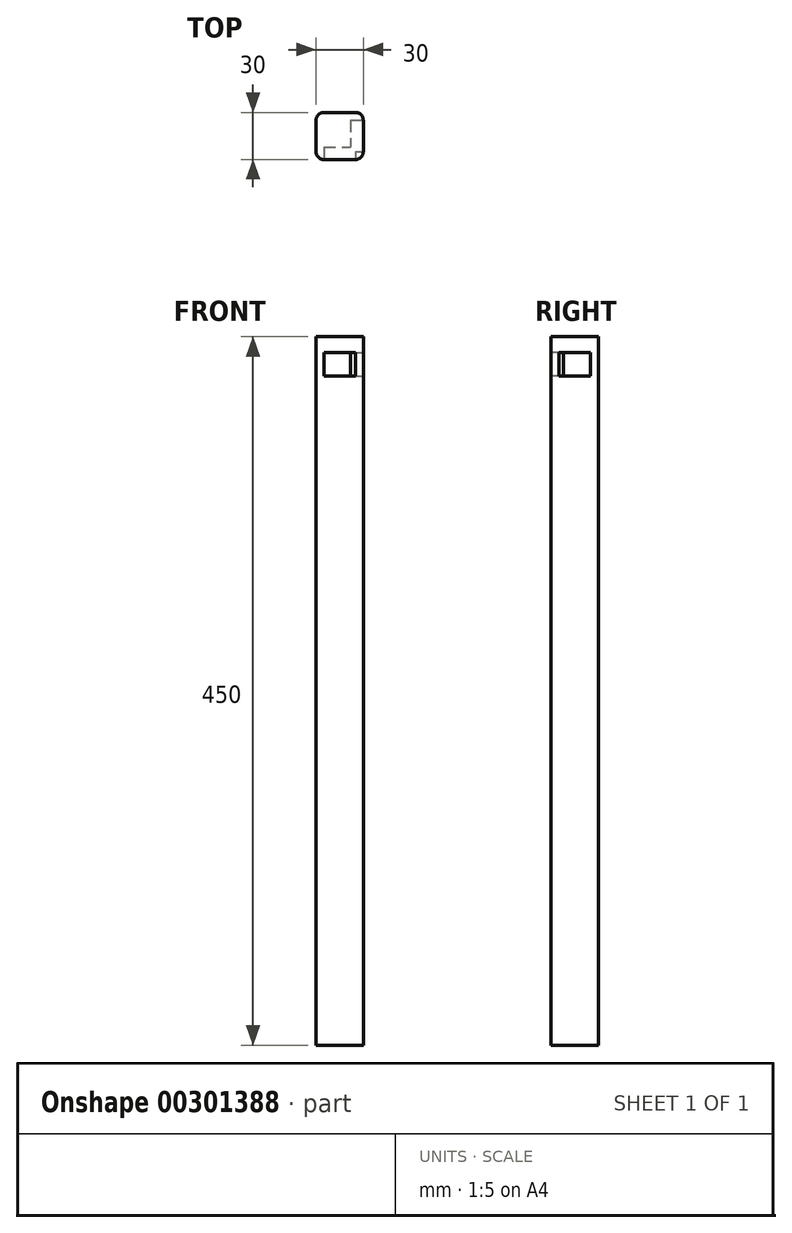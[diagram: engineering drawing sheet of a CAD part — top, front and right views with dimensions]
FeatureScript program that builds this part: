
annotation { "Feature Type Name" : "Feature", "Feature Type Description" : "" }
export const myFeature = defineFeature(function(context is Context, id is Id, definition is map)
    precondition{}
    {
        {
            var Q0;
            Q0=qCreatedBy(makeId("Top.planeOp"),FACE);
            var sketch = newSketch(context, id + "F0", { "sketchPlane" : qUnion([Q0])});
            skLineSegment(sketch, "E0.bottom", {"start": v(0, 0) * mm, "end": v(30, 0) * mm});
            skLineSegment(sketch, "E0.top", {"start": v(0, -30) * mm, "end": v(30, -30) * mm});
            skLineSegment(sketch, "E0.left", {"start": v(0, 0) * mm, "end": v(0, -30) * mm});
            skLineSegment(sketch, "E0.right", {"start": v(30, 0) * mm, "end": v(30, -30) * mm});
            skSolve(sketch);
        }
        {
            var Q0;
            Q0=makeQuery(id+"F0.imprint","IMPRINT",FACE,{"disambiguationData":[TD([[makeQuery(id+"F0.imprint","IMPRINT",EDGE,{"derivedFrom":sQuery(id+"F0.wireOp",EDGE,"E0.bottom")}),-1.0]])]});
            extrude(context, id + "F1", {"entities" : qUnion([Q0]), "depth" : 450 * mm});
        }
        {
            var Q0;
            Q0=makeQuery(id+"F1.opExtrude","SWEPT_FACE",FACE,{"disambiguationData":[OSD([sQuery(id+"F0.wireOp",EDGE,"E0.right")])]});
            var sketch = newSketch(context, id + "F2", { "sketchPlane" : qUnion([Q0])});
            skLineSegment(sketch, "E1", {"start": v(0, 440) * mm, "end": v(-5, 440) * mm});
            skLineSegment(sketch, "E2", {"start": v(-30, 440) * mm, "end": v(-25, 440) * mm});
            skLineSegment(sketch, "E3.bottom", {"start": v(-5, 440) * mm, "end": v(-25, 440) * mm});
            skLineSegment(sketch, "E3.top", {"start": v(-5, 425) * mm, "end": v(-25, 425) * mm});
            skLineSegment(sketch, "E3.left", {"start": v(-5, 440) * mm, "end": v(-5, 425) * mm});
            skLineSegment(sketch, "E3.right", {"start": v(-25, 440) * mm, "end": v(-25, 425) * mm});
            skLineSegment(sketch, "E4", {"start": v(-25.22, 450) * mm, "end": v(-25, 440) * mm});
            skSolve(sketch);
        }
        {
            var Q0;
            Q0=makeQuery(id+"F2.imprint","IMPRINT",FACE,{"disambiguationData":[TD([[makeQuery(id+"F2.imprint","IMPRINT",EDGE,{"derivedFrom":sQuery(id+"F2.wireOp",EDGE,"E3.bottom")}),1.0]])]});
            extrude(context, id + "F3", {"entities" : qUnion([Q0]), "operationType" : NewBodyOperationType.REMOVE, "oppositeDirection" : true, "depth" : 8 * mm});
        }
        {
            var Q0;
            Q0=makeQuery(id+"F1.opExtrude","SWEPT_FACE",FACE,{"disambiguationData":[OSD([sQuery(id+"F0.wireOp",EDGE,"E0.top")])]});
            var sketch = newSketch(context, id + "F4", { "sketchPlane" : qUnion([Q0])});
            skLineSegment(sketch, "E5", {"start": v(0, 440) * mm, "end": v(5, 440) * mm});
            skLineSegment(sketch, "E6", {"start": v(30, 440) * mm, "end": v(25, 440) * mm});
            skLineSegment(sketch, "E7.bottom", {"start": v(5, 440) * mm, "end": v(25, 440) * mm});
            skLineSegment(sketch, "E7.top", {"start": v(5, 425) * mm, "end": v(25, 425) * mm});
            skLineSegment(sketch, "E7.left", {"start": v(5, 440) * mm, "end": v(5, 425) * mm});
            skLineSegment(sketch, "E7.right", {"start": v(25, 440) * mm, "end": v(25, 425) * mm});
            skLineSegment(sketch, "E8", {"start": v(9.03, 440) * mm, "end": v(9.03, 450) * mm});
            skSolve(sketch);
        }
        {
            var Q0;
            Q0=makeQuery(id+"F4.imprint","IMPRINT",FACE,{"disambiguationData":[TD([[makeQuery(id+"F4.imprint","IMPRINT",EDGE,{"derivedFrom":sQuery(id+"F4.wireOp",EDGE,"E7.top")}),1.0]])]});
            extrude(context, id + "F5", {"entities" : qUnion([Q0]), "operationType" : NewBodyOperationType.REMOVE, "oppositeDirection" : true, "depth" : 8 * mm});
        }
        {
            var Q0;
            Q0=makeQuery(id+"F1.opExtrude","SWEPT_EDGE",EDGE,{"disambiguationData":[OSD([sQuery(id+"F0.wireOp",EDGE,"E0.top"),sQuery(id+"F0.wireOp",EDGE,"E0.right")])]});
            var Q1;
            Q1=makeQuery(id+"F1.opExtrude","SWEPT_EDGE",EDGE,{"disambiguationData":[OSD([sQuery(id+"F0.wireOp",EDGE,"E0.bottom"),sQuery(id+"F0.wireOp",EDGE,"E0.right")])]});
            var Q2;
            Q2=makeQuery(id+"F1.opExtrude","SWEPT_EDGE",EDGE,{"disambiguationData":[OSD([sQuery(id+"F0.wireOp",EDGE,"E0.bottom"),sQuery(id+"F0.wireOp",EDGE,"E0.left")])]});
            var Q3;
            Q3=makeQuery(id+"F1.opExtrude","SWEPT_EDGE",EDGE,{"disambiguationData":[OSD([sQuery(id+"F0.wireOp",EDGE,"E0.top"),sQuery(id+"F0.wireOp",EDGE,"E0.left")])]});
            fillet(context, id + "F6", {"entities" : qUnion([Q0, Q1, Q2, Q3]), "radius" : 5 * mm, "tangentPropagation" : true, "allowEdgeOverflow" : false});
        }
    });
